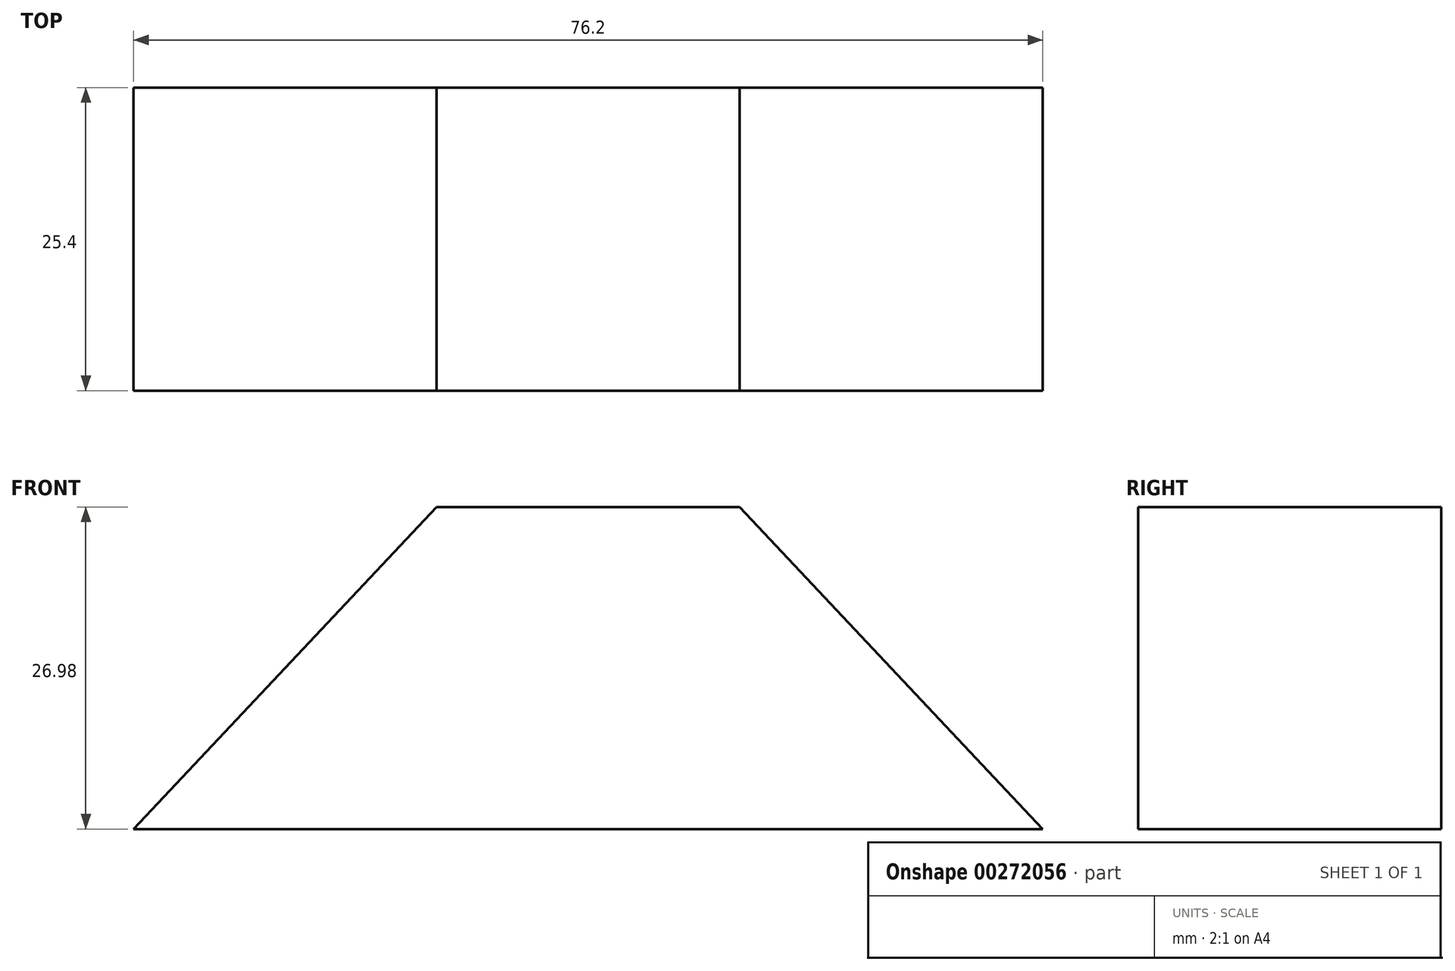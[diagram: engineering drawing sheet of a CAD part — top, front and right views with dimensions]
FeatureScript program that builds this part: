
annotation { "Feature Type Name" : "Feature", "Feature Type Description" : "" }
export const myFeature = defineFeature(function(context is Context, id is Id, definition is map)
    precondition{}
    {
        {
            var Q0;
            Q0=qCreatedBy(makeId("Front.planeOp"),FACE);
            var sketch = newSketch(context, id + "F0", { "sketchPlane" : qUnion([Q0])});
            skLineSegment(sketch, "E0.bottom", {"start": v(-13.05, 13.5) * mm, "end": v(12.35, 13.5) * mm});
            skLineSegment(sketch, "E0.top", {"start": v(-12.35, -13.5) * mm, "end": v(13.05, -13.5) * mm});
            skPoint(sketch, "E0.middle", {"position": v(0, 0) * mm});
            skLineSegment(sketch, "E1", {"start": v(12.35, 13.5) * mm, "end": v(37.75, -13.5) * mm});
            skLineSegment(sketch, "E2", {"start": v(-13.05, 13.5) * mm, "end": v(-38.45, -13.5) * mm});
            skLineSegment(sketch, "E3", {"start": v(-38.45, -13.5) * mm, "end": v(37.75, -13.5) * mm});
            skSolve(sketch);
        }
        {
            var Q0;
            Q0 = qSketchRegion(id + "F0", true);
            extrude(context, id + "F1", {"entities" : qUnion([Q0]), "depth" : 25.4 * mm});
        }
    });
